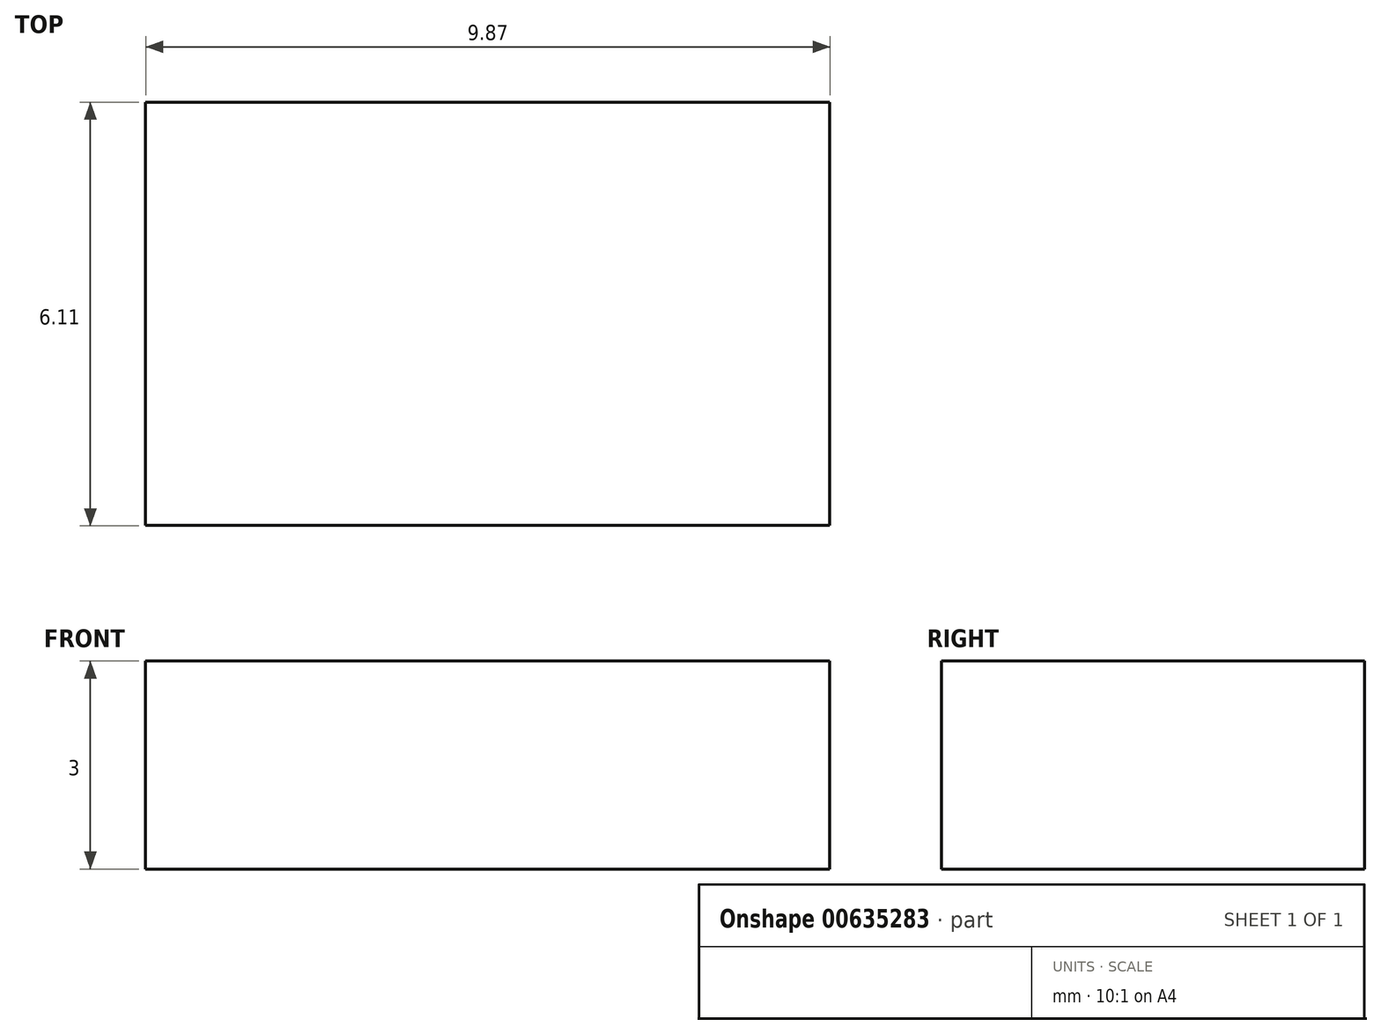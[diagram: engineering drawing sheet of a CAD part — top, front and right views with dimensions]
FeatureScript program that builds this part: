
annotation { "Feature Type Name" : "Feature", "Feature Type Description" : "" }
export const myFeature = defineFeature(function(context is Context, id is Id, definition is map)
    precondition{}
    {
        {
            var Q0;
            Q0=qCreatedBy(makeId("Top.planeOp"),FACE);
            var sketch = newSketch(context, id + "F0", { "sketchPlane" : qUnion([Q0])});
            skLineSegment(sketch, "E0.bottom", {"start": v(-5.53, 6.94) * mm, "end": v(-15.4, 6.94) * mm});
            skLineSegment(sketch, "E0.top", {"start": v(-5.53, 13.05) * mm, "end": v(-15.4, 13.05) * mm});
            skLineSegment(sketch, "E0.left", {"start": v(-5.53, 6.94) * mm, "end": v(-5.53, 13.05) * mm});
            skLineSegment(sketch, "E0.right", {"start": v(-15.4, 6.94) * mm, "end": v(-15.4, 13.05) * mm});
            skPoint(sketch, "E0.middle", {"position": v(-10.47, 10) * mm});
            skSolve(sketch);
        }
        {
            var Q0;
            Q0=makeQuery(id+"F0.imprint","IMPRINT",FACE,{"disambiguationData":[TD([[makeQuery(id+"F0.imprint","IMPRINT",EDGE,{"derivedFrom":sQuery(id+"F0.wireOp",EDGE,"E0.bottom")}),-1.0]])]});
            extrude(context, id + "F1", {"entities" : qUnion([Q0]), "depth" : 3 * mm, "offsetDistance" : 25 * mm});
        }
    });
